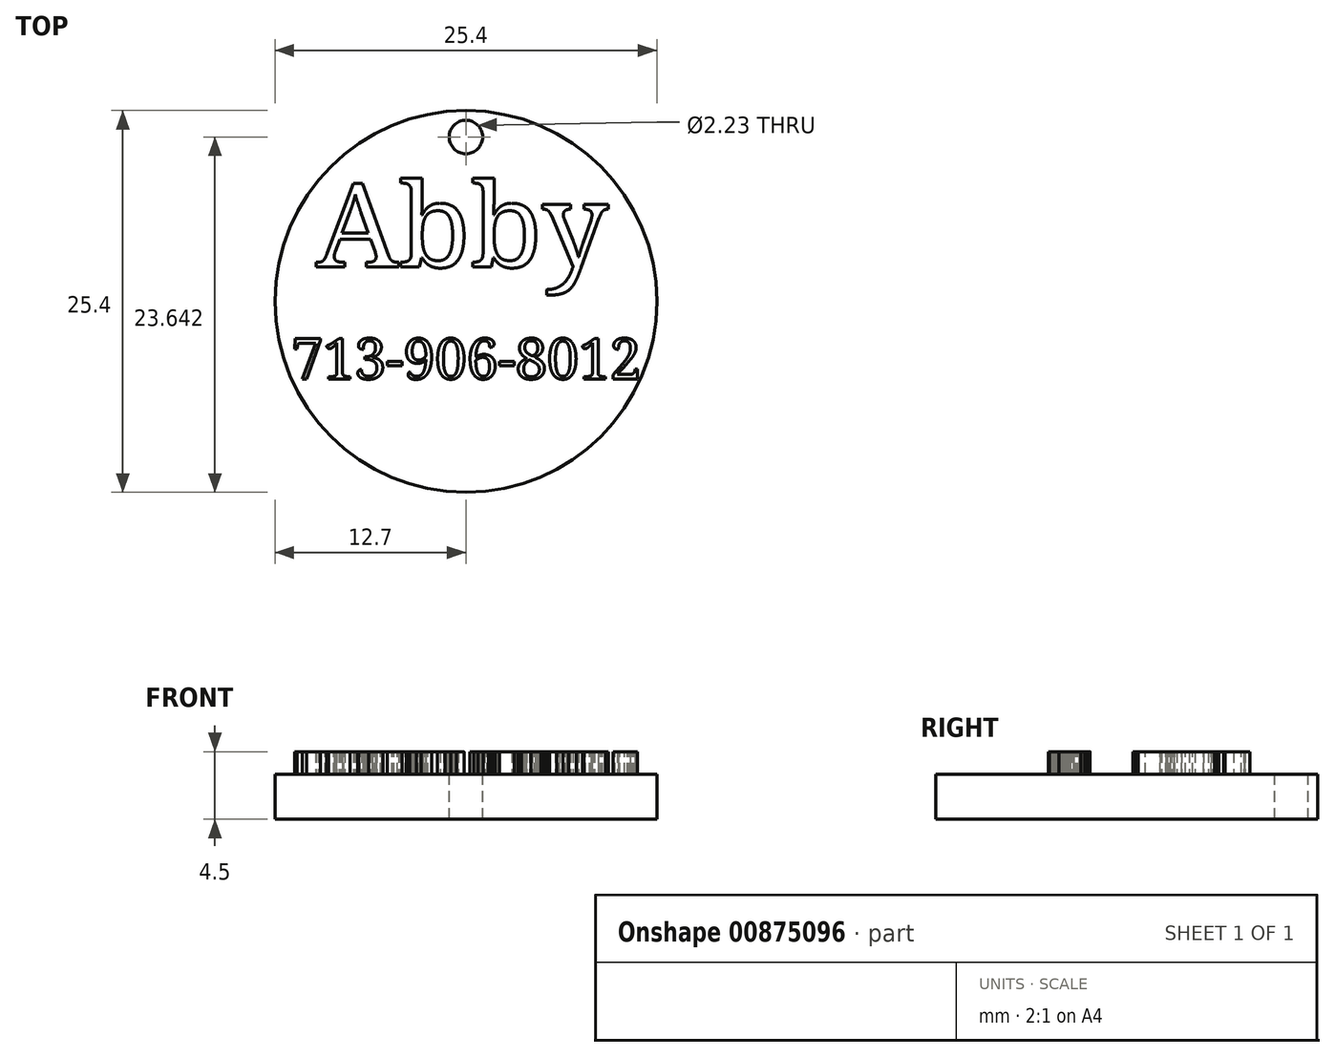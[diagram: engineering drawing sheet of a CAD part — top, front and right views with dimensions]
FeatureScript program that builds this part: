
annotation { "Feature Type Name" : "Feature", "Feature Type Description" : "" }
export const myFeature = defineFeature(function(context is Context, id is Id, definition is map)
    precondition{}
    {
        {
            var Q0;
            Q0=qCreatedBy(makeId("Top.planeOp"),FACE);
            var sketch = newSketch(context, id + "F0", { "sketchPlane" : qUnion([Q0])});
            skCircle(sketch, "E0", {"center": v(0, 0) * mm, "radius": 12.7 * mm});
            skSolve(sketch);
        }
        {
            var Q0;
            Q0=makeQuery(id+"F0.imprint","IMPRINT",FACE,{"disambiguationData":[TD([[makeQuery(id+"F0.imprint","IMPRINT",EDGE,{"derivedFrom":sQuery(id+"F0.wireOp",EDGE,"E0")}),1.0]])]});
            extrude(context, id + "F1", {"entities" : qUnion([Q0]), "depth" : 3 * mm, "offsetDistance" : 25 * mm});
        }
        {
            var Q0;
            Q0=makeQuery(id+"F1.opExtrude","CAP_FACE",FACE,{"disambiguationData":[OSD([sQuery(id+"F0.wireOp",EDGE,"E0")])],"isStart":false});
            var sketch = newSketch(context, id + "F2", { "sketchPlane" : qUnion([Q0])});
            skText(sketch, "E1", { "text": "Abby", "fontName": "NotoSerif-Regular.ttf"});
            const initialGuessF2  = {"E1": [-0.00996, 0.00229, 1, 0, 0.0056]};
            skSetInitialGuess(sketch, initialGuessF2);
            skSolve(sketch);
        }
        {
            var Q0;
            Q0 = qSketchRegion(id + "F2", true);
            extrude(context, id + "F3", {"entities" : qUnion([Q0]), "operationType" : NewBodyOperationType.ADD, "depth" : 1.5 * mm, "offsetDistance" : 25 * mm});
        }
        {
            var Q0;
            {var subQ0=sQuery(id+"F0.wireOp",EDGE,"E0");Q0=makeQuery(id+"F3.boolean.opBoolean","SPLIT",FACE,{"disambiguationData":[TD([makeQuery(id+"F1.opExtrude","SWEPT_FACE",FACE,{"disambiguationData":[OSD([subQ0])]})])],"derivedFrom":makeQuery(id+"F1.opExtrude","CAP_FACE",FACE,{"disambiguationData":[OSD([subQ0])],"isStart":false})});}
            var sketch = newSketch(context, id + "F4", { "sketchPlane" : qUnion([Q0])});
            skText(sketch, "E2", { "text": "713-906-8012", "fontName": "NotoSerif-Regular.ttf"});
            const initialGuessF4  = {"E2": [-0.0116, -0.00515, 1, 0, 0.0027]};
            skSetInitialGuess(sketch, initialGuessF4);
            skSolve(sketch);
        }
        {
            var Q0;
            Q0 = qSketchRegion(id + "F4", true);
            var Q1;
            Q1 = qSketchRegion(id + "F6", true);
            extrude(context, id + "F5", {"entities" : qUnion([Q0, Q1]), "operationType" : NewBodyOperationType.ADD, "depth" : 1.5 * mm, "offsetDistance" : 25 * mm});
        }
        {
            var Q0;
            {var subQ41=sQuery(id+"F0.wireOp",EDGE,"E0");var subQ42=makeQuery(id+"F1.opExtrude","SWEPT_FACE",FACE,{"disambiguationData":[OSD([subQ41])]});Q0=makeQuery(id+"F5.boolean.opBoolean","SPLIT",FACE,{"disambiguationData":[TD([subQ42])],"derivedFrom":makeQuery(id+"F3.boolean.opBoolean","SPLIT",FACE,{"disambiguationData":[TD([subQ42])],"derivedFrom":makeQuery(id+"F1.opExtrude","CAP_FACE",FACE,{"disambiguationData":[OSD([subQ41])],"isStart":false})})});}
            var sketch = newSketch(context, id + "F6", { "sketchPlane" : qUnion([Q0])});
            skCircle(sketch, "E3", {"center": v(0, 10.94) * mm, "radius": 1.11 * mm});
            skSolve(sketch);
        }
        {
            var Q0;
            Q0=makeQuery(id+"F6.imprint","IMPRINT",FACE,{"disambiguationData":[TD([[makeQuery(id+"F6.imprint","IMPRINT",EDGE,{"derivedFrom":sQuery(id+"F6.wireOp",EDGE,"E3")}),1.0]])]});
            extrude(context, id + "F7", {"entities" : qUnion([Q0]), "operationType" : NewBodyOperationType.REMOVE, "endBound" : BoundingType.THROUGH_ALL, "oppositeDirection" : true, "depth" : 25 * mm, "offsetDistance" : 25 * mm});
        }
    });
